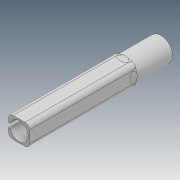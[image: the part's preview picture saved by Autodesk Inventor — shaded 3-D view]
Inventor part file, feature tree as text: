
AUTODESK INVENTOR PART (.ipt)
format: ipt  version: 2017 (Build 210142000, 142)  size: 192,000 bytes
history: native  units: mm
features: extrude x4, sketch x4, fillet x2, other x1
ambient origin geometry x8: Origin, YZ Plane, XZ Plane, XY Plane, X Axis, Y Axis, Z Axis, Center Point
bodies: Body1 (feature_tree)
feature tree (11):
  other  "Sólido1"
  extrude  "Extrusión1"  Depth=6.0mm
  extrude  "Extrusión2"  Depth=8.0mm
  extrude  "Extrusión3"  Depth=6.2mm
  extrude  "Extrusión4"  Depth=1.5mm
  fillet  "Empalme2"  Radius=10.0mm
  fillet  "Empalme3"  Radius=1.5mm
  sketch  "Boceto1"  dims[d0=10.0mm d1=6.0mm]
  sketch  "Boceto2"  dims[d2=36.0mm d3=0.0mm d4=8.0mm]
  sketch  "Boceto3"  dims[d5=12.0mm d6=0.0mm d7=6.2mm]
  sketch  "Boceto4"  dims[d8=10.0mm d9=0.0mm d11=1.5mm d12=10.0mm d13=0.0mm d14=1.5mm d15=4.0mm]
